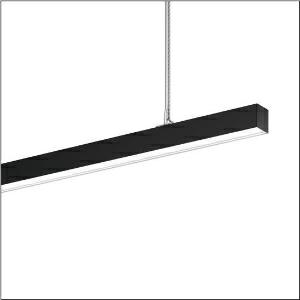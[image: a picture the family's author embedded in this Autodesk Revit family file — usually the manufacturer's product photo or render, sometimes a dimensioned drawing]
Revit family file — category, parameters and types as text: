
# Revit family: silica_r__21_51mx30tbt5b_11dd
name_source: partatom
category: Lighting Fixtures
units: mm (PartAtom-declared; Revit-internal decimal feet)

## family parameters
Cut with Voids When Loaded = No
Host = Face
Light Source = No
Part Type = Normal
Room Calculation Point = No
Round Connector Dimension = Use Diameter
Shared = No

## types (1)
- --- (1 x LED, 5150 lm, 42.2 W, 6500K)
    Apparent Load = 42 VA
    CIE Flux Codes = 47 79 96 58 100
    Color Rendering = 80
    Color Temperature = 6500K
    Default Elevation = 1800 mm
    Description = Silica® 21, office luminaire, primary optical cover: cover, of PMMA, opal, light emission: direct/indirect distribution, primary light characteristic: symmetric, installation type: suspended mounting, LED, rated luminous flux: 5.150lm, luminous efficacy: 116lm/W, light colour: 8tw, colour temperature: 2700..6500K, control gear: ECG DALI, with terminal, 3+2-pole, max. 2.5mm², mains connection: 220..240V, AC, 50/60Hz, rated input power: 44.3W, luminaire housing, of aluminium, jet black (RAL 9005), length: 1.504mm, width: 53mm, height: 53mm, protection rating (complete): IP20, insulation class (complete): insulation class I (protective earthing), certification: CE, permissible operating ambient temperature: 0..+35°C, standard: EN 50419, packaging unit: 1 piece
    Height = 53 mm
    Lamp = 1 x LED
    Lamp Light Flux = 5150 lm
    Lamp Power = 42.2 W
    Lamp count = 1
    Length = 1504 mm
    Luminous efficacy = 122 lm/W
    Manufacturer = Siteco
    ModVariant = No
    Model = 51MX30TBT5B
    Mounting Place = Ceiling
    Mounting Type = Pendant
    Number of Poles = 1
    OnlyDefault = Yes
    Power Factor = 1
    Product Name = Silica® 21
    Product group = office luminaire | ceiling pendant
    ProductGroupID = 902
    Protection Class = Protection class I
    Protection Degree = IP 20
    RLX_Detail_Level = 1
    RLX_Emergency_Light_Flux = 0 lm
    RLX_Emergency_Type = 0
    RLX_Emergency_Type_DB = No
    RlxData = <blob elided: 22901 chars, md5=7ecad14c>
    Socket = socket
    Standby Power = 0 W
    System Light Flux = 5150 lm
    System Power = 42 W
    Type Comments = individual setting
    Type Image = l_1335856.jpg
    URL = http://relux.com
    VarID = @adj_109435
    Voltage = 0 V
    Weight = 0.00 kg
    Width = 53 mm

## geometry (parser evidence)
native form markers: Blend x4, Sweep x11
no freeform markers — native parametric forms only
